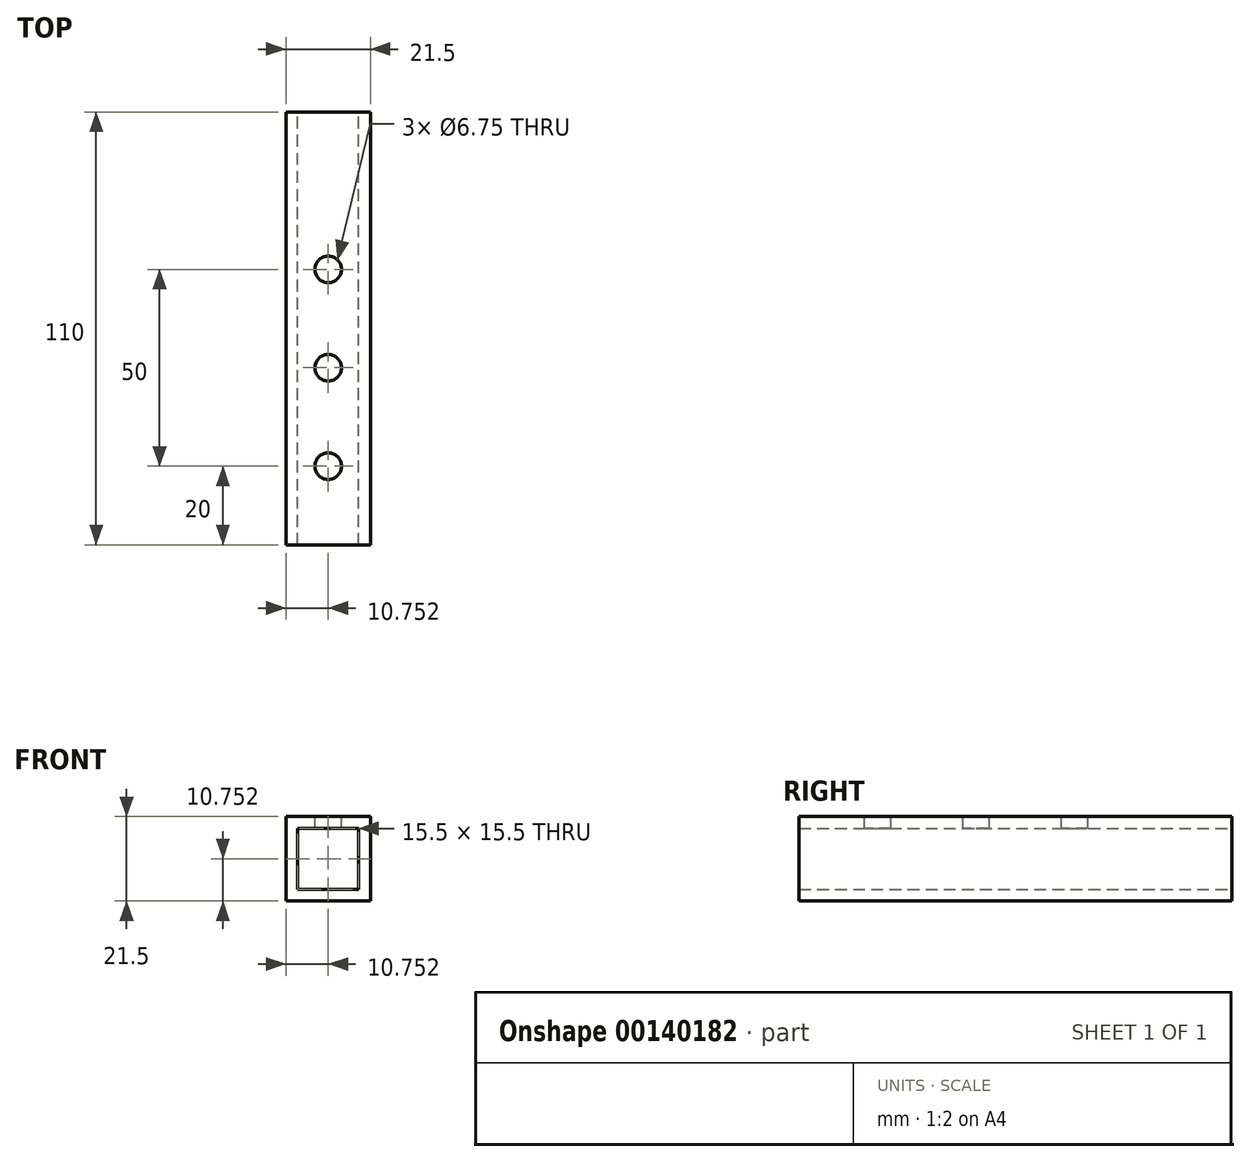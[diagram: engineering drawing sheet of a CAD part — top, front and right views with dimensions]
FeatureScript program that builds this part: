
annotation { "Feature Type Name" : "Feature", "Feature Type Description" : "" }
export const myFeature = defineFeature(function(context is Context, id is Id, definition is map)
    precondition{}
    {
        {
            var Q0;
            Q0=qCreatedBy(makeId("Front.planeOp"),FACE);
            var sketch = newSketch(context, id + "F0", { "sketchPlane" : qUnion([Q0])});
            skLineSegment(sketch, "E0.bottom", {"start": v(-69.47, 59.21) * mm, "end": v(-53.97, 59.21) * mm});
            skLineSegment(sketch, "E0.top", {"start": v(-69.47, 43.71) * mm, "end": v(-53.97, 43.71) * mm});
            skLineSegment(sketch, "E0.left", {"start": v(-69.47, 59.21) * mm, "end": v(-69.47, 43.71) * mm});
            skLineSegment(sketch, "E0.right", {"start": v(-53.97, 59.21) * mm, "end": v(-53.97, 43.71) * mm});
            skLineSegment(sketch, "E1.bottom", {"start": v(-72.47, 62.21) * mm, "end": v(-50.97, 62.21) * mm});
            skLineSegment(sketch, "E1.top", {"start": v(-72.47, 40.71) * mm, "end": v(-50.97, 40.71) * mm});
            skLineSegment(sketch, "E1.left", {"start": v(-72.47, 62.21) * mm, "end": v(-72.47, 40.71) * mm});
            skLineSegment(sketch, "E1.right", {"start": v(-50.97, 62.21) * mm, "end": v(-50.97, 40.71) * mm});
            skSolve(sketch);
        }
        {
            var Q0;
            Q0 = qSketchRegion(id + "F0", true);
            extrude(context, id + "F1", {"entities" : qUnion([Q0]), "depth" : 110 * mm});
        }
        {
            var Q0;
            Q0=makeQuery(id+"F1.opExtrude","SWEPT_FACE",FACE,{"disambiguationData":[OSD([sQuery(id+"F0.wireOp",EDGE,"E1.bottom")])]});
            var sketch = newSketch(context, id + "F2", { "sketchPlane" : qUnion([Q0])});
            skCircle(sketch, "E2", {"center": v(-61.72, -90) * mm, "radius": 3.38 * mm});
            skCircle(sketch, "E3", {"center": v(-61.72, -65) * mm, "radius": 3.38 * mm});
            skCircle(sketch, "E4", {"center": v(-61.72, -40) * mm, "radius": 3.38 * mm});
            skSolve(sketch);
        }
        {
            var Q0;
            Q0 = qSketchRegion(id + "F2", true);
            extrude(context, id + "F3", {"entities" : qUnion([Q0]), "operationType" : NewBodyOperationType.REMOVE, "oppositeDirection" : true, "depth" : 5 * mm});
        }
    });
